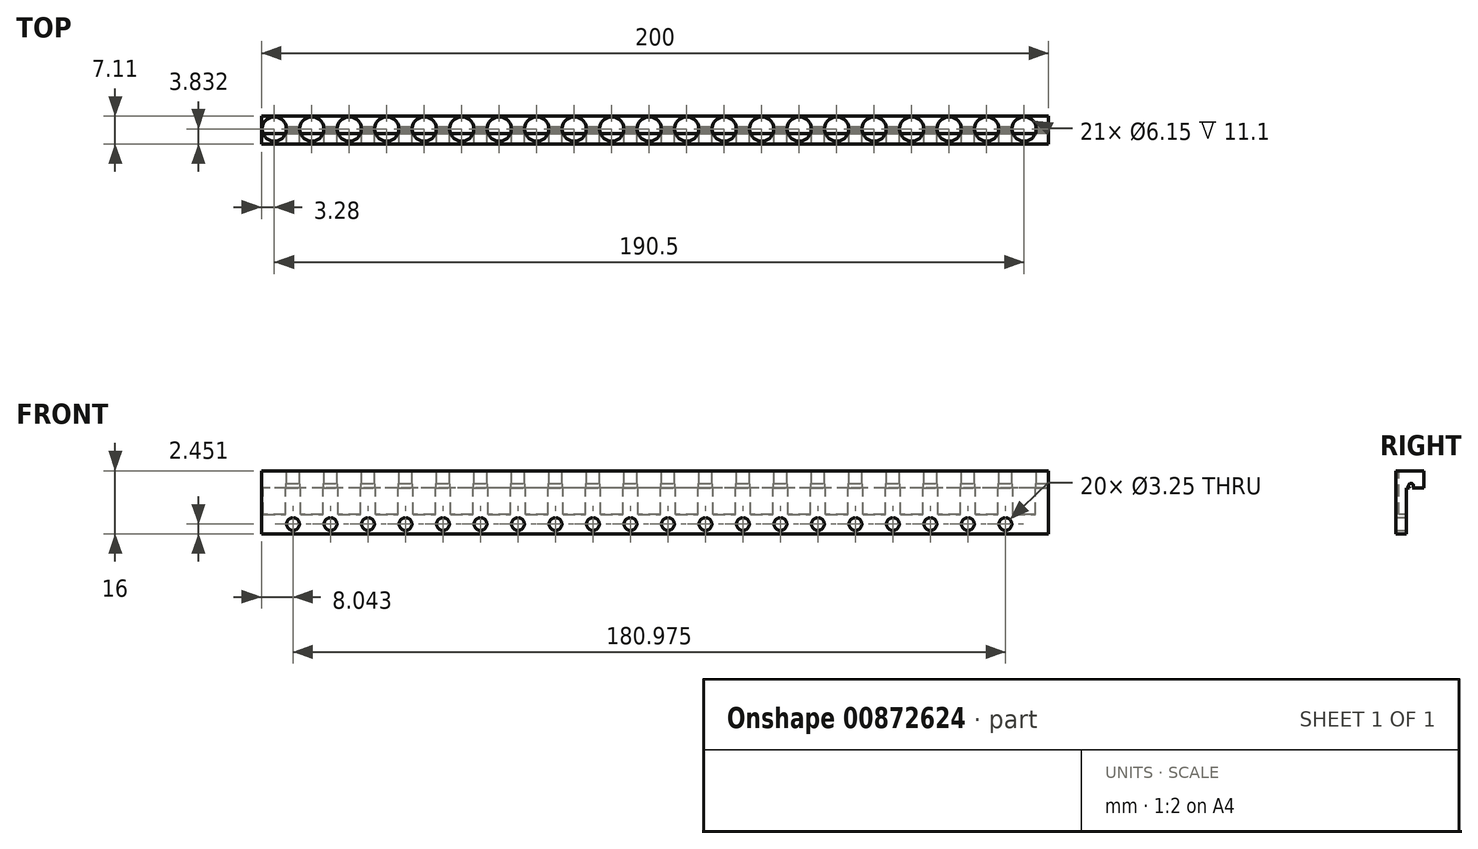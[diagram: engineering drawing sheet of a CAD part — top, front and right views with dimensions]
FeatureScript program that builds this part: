
annotation { "Feature Type Name" : "Feature", "Feature Type Description" : "" }
export const myFeature = defineFeature(function(context is Context, id is Id, definition is map)
    precondition{}
    {
        {
            var Q0;
            Q0=qCreatedBy(makeId("Right.planeOp"),FACE);
            var sketch = newSketch(context, id + "F0", { "sketchPlane" : qUnion([Q0])});
            skLineSegment(sketch, "E0.bottom", {"start": v(0, 0) * mm, "end": v(2.64, 0) * mm});
            skLineSegment(sketch, "E0.left", {"start": v(0, 0) * mm, "end": v(0, 16) * mm});
            skLineSegment(sketch, "E0.right", {"start": v(2.64, 0) * mm, "end": v(2.64, 11.68) * mm});
            skLineSegment(sketch, "E1.bottom", {"start": v(0, 16) * mm, "end": v(7.11, 16) * mm});
            skLineSegment(sketch, "E1.top", {"start": v(2.64, 11.68) * mm, "end": v(7.11, 11.68) * mm});
            skLineSegment(sketch, "E1.right", {"start": v(7.11, 16) * mm, "end": v(7.11, 11.68) * mm});
            skSolve(sketch);
        }
        {
            var Q0;
            Q0=qSketchRegion(id+"F0",true);
            extrude(context, id + "F1", {"entities" : qUnion([Q0]), "depth" : 200 * mm});
        }
        {
            var Q0;
            Q0=makeQuery(id+"F1.opExtrude","SWEPT_FACE",FACE,{"disambiguationData":[OSD([sQuery(id+"F0.wireOp",EDGE,"E1.bottom")])]});
            var sketch = newSketch(context, id + "F2", { "sketchPlane" : qUnion([Q0])});
            skCircle(sketch, "E2", {"center": v(3.28, 3.83) * mm, "radius": 3.08 * mm});
            skCircle(sketch, "E3.1.0.0", {"center": v(12.8, 3.83) * mm, "radius": 3.08 * mm});
            skCircle(sketch, "E3.2.0.0", {"center": v(22.33, 3.83) * mm, "radius": 3.08 * mm});
            skCircle(sketch, "E3.3.0.0", {"center": v(31.86, 3.83) * mm, "radius": 3.08 * mm});
            skCircle(sketch, "E3.4.0.0", {"center": v(41.38, 3.83) * mm, "radius": 3.08 * mm});
            skCircle(sketch, "E3.5.0.0", {"center": v(50.9, 3.83) * mm, "radius": 3.08 * mm});
            skCircle(sketch, "E3.6.0.0", {"center": v(60.43, 3.83) * mm, "radius": 3.08 * mm});
            skCircle(sketch, "E3.7.0.0", {"center": v(69.95, 3.83) * mm, "radius": 3.08 * mm});
            skCircle(sketch, "E3.8.0.0", {"center": v(79.48, 3.83) * mm, "radius": 3.08 * mm});
            skCircle(sketch, "E3.9.0.0", {"center": v(89, 3.83) * mm, "radius": 3.08 * mm});
            skLineSegment(sketch, "E3.direction1", {"start": v(3.28, 3.83) * mm, "end": v(12.8, 3.83) * mm, "construction": true});
            skCircle(sketch, "E4.0.10.0", {"center": v(98.53, 3.83) * mm, "radius": 3.08 * mm});
            skCircle(sketch, "E4.0.11.0", {"center": v(108.06, 3.83) * mm, "radius": 3.08 * mm});
            skCircle(sketch, "E4.0.12.0", {"center": v(117.58, 3.83) * mm, "radius": 3.08 * mm});
            skCircle(sketch, "E4.0.13.0", {"center": v(127.1, 3.83) * mm, "radius": 3.08 * mm});
            skCircle(sketch, "E4.0.14.0", {"center": v(136.63, 3.83) * mm, "radius": 3.08 * mm});
            skCircle(sketch, "E4.0.15.0", {"center": v(146.16, 3.83) * mm, "radius": 3.08 * mm});
            skCircle(sketch, "E4.0.16.0", {"center": v(155.68, 3.83) * mm, "radius": 3.08 * mm});
            skCircle(sketch, "E4.0.17.0", {"center": v(165.2, 3.83) * mm, "radius": 3.08 * mm});
            skCircle(sketch, "E4.0.18.0", {"center": v(174.73, 3.83) * mm, "radius": 3.08 * mm});
            skCircle(sketch, "E4.0.19.0", {"center": v(184.25, 3.83) * mm, "radius": 3.08 * mm});
            skCircle(sketch, "E5.0.20.0", {"center": v(193.78, 3.83) * mm, "radius": 3.08 * mm});
            skSolve(sketch);
        }
        {
            var Q0;
            Q0=qSketchRegion(id+"F2",true);
            extrude(context, id + "F3", {"entities" : qUnion([Q0]), "operationType" : NewBodyOperationType.REMOVE, "oppositeDirection" : true, "depth" : 11.1 * mm});
        }
        {
            var Q0;
            Q0=makeQuery(id+"F1.opExtrude","CAP_FACE",FACE,{"disambiguationData":[OSD([sQuery(id+"F0.wireOp",EDGE,"E0.bottom"),sQuery(id+"F0.wireOp",EDGE,"E0.left"),sQuery(id+"F0.wireOp",EDGE,"E0.right"),sQuery(id+"F0.wireOp",EDGE,"E1.bottom"),sQuery(id+"F0.wireOp",EDGE,"E1.top"),sQuery(id+"F0.wireOp",EDGE,"E1.right")])],"isStart":false});
            var sketch = newSketch(context, id + "F4", { "sketchPlane" : qUnion([Q0])});
            skCircle(sketch, "E6", {"center": v(3.83, 12.18) * mm, "radius": 0.64 * mm});
            skSolve(sketch);
        }
        {
            var Q0;
            Q0=qSketchRegion(id+"F4",true);
            extrude(context, id + "F5", {"entities" : qUnion([Q0]), "operationType" : NewBodyOperationType.REMOVE, "endBound" : BoundingType.THROUGH_ALL, "oppositeDirection" : true, "depth" : 25 * mm});
        }
        {
            var Q0;
            Q0=makeQuery(id+"F1.opExtrude","SWEPT_FACE",FACE,{"disambiguationData":[OSD([sQuery(id+"F0.wireOp",EDGE,"E0.right")])]});
            var sketch = newSketch(context, id + "F6", { "sketchPlane" : qUnion([Q0])});
            skLineSegment(sketch, "E7", {"start": v(-190.94, 4.9) * mm, "end": v(-187.1, 4.9) * mm, "construction": true});
            skLineSegment(sketch, "E8", {"start": v(-189.02, 4.9) * mm, "end": v(-189.02, 0) * mm, "construction": true});
            skLineSegment(sketch, "E9", {"start": v(-189.02, 2.45) * mm, "end": v(-195.84, 2.45) * mm, "construction": true});
            skCircle(sketch, "E10", {"center": v(-189.02, 2.45) * mm, "radius": 1.63 * mm});
            skCircle(sketch, "E11.1.0.0", {"center": v(-179.5, 2.45) * mm, "radius": 1.63 * mm});
            skCircle(sketch, "E11.2.0.0", {"center": v(-169.97, 2.45) * mm, "radius": 1.63 * mm});
            skCircle(sketch, "E11.3.0.0", {"center": v(-160.44, 2.45) * mm, "radius": 1.63 * mm});
            skCircle(sketch, "E11.4.0.0", {"center": v(-150.92, 2.45) * mm, "radius": 1.63 * mm});
            skCircle(sketch, "E11.5.0.0", {"center": v(-141.4, 2.45) * mm, "radius": 1.63 * mm});
            skCircle(sketch, "E11.6.0.0", {"center": v(-131.87, 2.45) * mm, "radius": 1.63 * mm});
            skCircle(sketch, "E11.7.0.0", {"center": v(-122.34, 2.45) * mm, "radius": 1.63 * mm});
            skCircle(sketch, "E11.8.0.0", {"center": v(-112.82, 2.45) * mm, "radius": 1.63 * mm});
            skCircle(sketch, "E11.9.0.0", {"center": v(-103.3, 2.45) * mm, "radius": 1.63 * mm});
            skCircle(sketch, "E11.10.0.0", {"center": v(-93.77, 2.45) * mm, "radius": 1.63 * mm});
            skCircle(sketch, "E11.11.0.0", {"center": v(-84.24, 2.45) * mm, "radius": 1.63 * mm});
            skCircle(sketch, "E11.12.0.0", {"center": v(-74.72, 2.45) * mm, "radius": 1.63 * mm});
            skCircle(sketch, "E11.13.0.0", {"center": v(-65.2, 2.45) * mm, "radius": 1.63 * mm});
            skCircle(sketch, "E11.14.0.0", {"center": v(-55.67, 2.45) * mm, "radius": 1.63 * mm});
            skCircle(sketch, "E11.15.0.0", {"center": v(-46.14, 2.45) * mm, "radius": 1.63 * mm});
            skCircle(sketch, "E11.16.0.0", {"center": v(-36.62, 2.45) * mm, "radius": 1.63 * mm});
            skCircle(sketch, "E11.17.0.0", {"center": v(-27.1, 2.45) * mm, "radius": 1.63 * mm});
            skCircle(sketch, "E11.18.0.0", {"center": v(-17.57, 2.45) * mm, "radius": 1.63 * mm});
            skCircle(sketch, "E11.19.0.0", {"center": v(-8.04, 2.45) * mm, "radius": 1.63 * mm});
            skLineSegment(sketch, "E11.direction1", {"start": v(-189.02, 2.45) * mm, "end": v(-179.5, 2.45) * mm, "construction": true});
            skSolve(sketch);
        }
        {
            var Q0;
            Q0=qSketchRegion(id+"F6",true);
            extrude(context, id + "F7", {"entities" : qUnion([Q0]), "operationType" : NewBodyOperationType.REMOVE, "endBound" : BoundingType.THROUGH_ALL, "oppositeDirection" : true, "depth" : 25 * mm});
        }
    });
